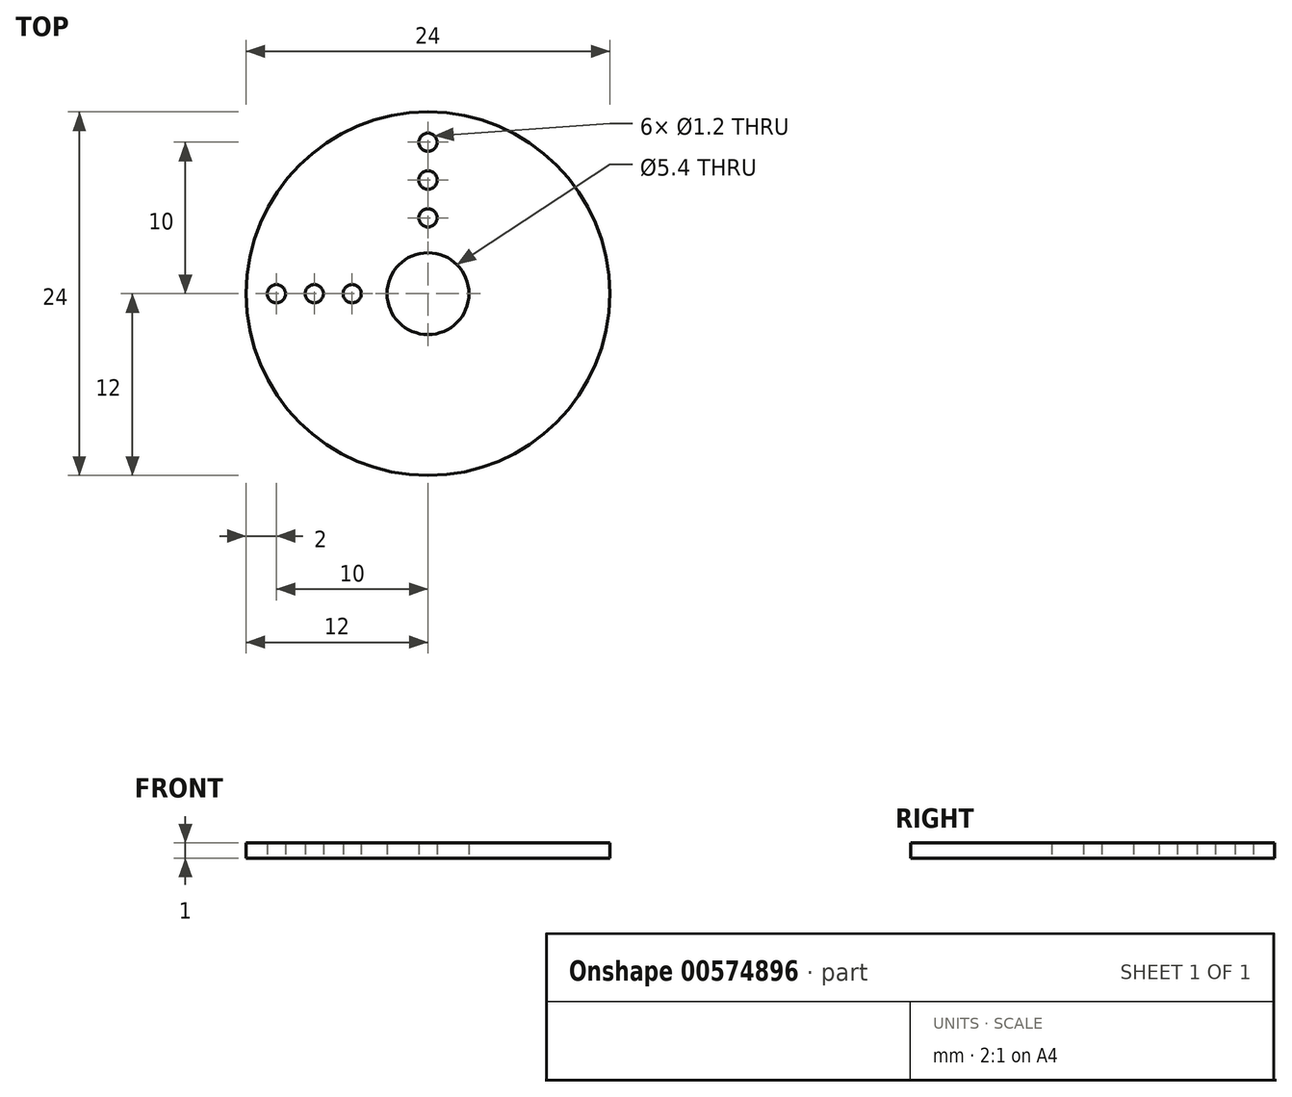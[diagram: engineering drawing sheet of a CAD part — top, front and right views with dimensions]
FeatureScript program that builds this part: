
annotation { "Feature Type Name" : "Feature", "Feature Type Description" : "" }
export const myFeature = defineFeature(function(context is Context, id is Id, definition is map)
    precondition{}
    {
        {
            var Q0;
            Q0=qCreatedBy(makeId("Top.planeOp"),FACE);
            var sketch = newSketch(context, id + "F0", { "sketchPlane" : qUnion([Q0])});
            skCircle(sketch, "E0", {"center": v(0, 0) * mm, "radius": 12 * mm});
            skCircle(sketch, "E1", {"center": v(0, 0) * mm, "radius": 2.7 * mm});
            skCircle(sketch, "E2", {"center": v(-5, 0) * mm, "radius": 0.6 * mm});
            skCircle(sketch, "E3.1.0.0", {"center": v(-7.5, 0) * mm, "radius": 0.6 * mm});
            skLineSegment(sketch, "E3.direction1", {"start": v(-5, 0) * mm, "end": v(-7.5, 0) * mm, "construction": true});
            skLineSegment(sketch, "E4", {"start": v(0, 0) * mm, "end": v(-12.52, 0) * mm, "construction": true});
            skLineSegment(sketch, "E5", {"start": v(0, 0) * mm, "end": v(-8.95, 8.95) * mm, "construction": true});
            skCircle(sketch, "E6.MirrorC", {"center": v(0, 5) * mm, "radius": 0.6 * mm});
            skCircle(sketch, "E7.MirrorC", {"center": v(0, 7.5) * mm, "radius": 0.6 * mm});
            skCircle(sketch, "E8.0.2.0", {"center": v(-10, 0) * mm, "radius": 0.6 * mm});
            skCircle(sketch, "E9.MirrorC", {"center": v(0, 10) * mm, "radius": 0.6 * mm});
            skSolve(sketch);
        }
        {
            var Q0;
            Q0=makeQuery(id+"F0.imprint","IMPRINT",FACE,{"disambiguationData":[TD([[makeQuery(id+"F0.imprint","IMPRINT",EDGE,{"derivedFrom":sQuery(id+"F0.wireOp",EDGE,"E0")}),1.0]])]});
            extrude(context, id + "F1", {"entities" : qUnion([Q0]), "depth" : 1 * mm, "offsetDistance" : 25 * mm});
        }
    });
